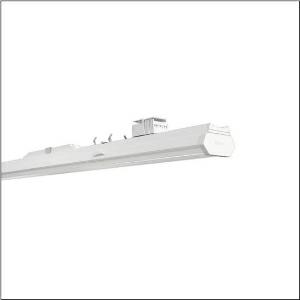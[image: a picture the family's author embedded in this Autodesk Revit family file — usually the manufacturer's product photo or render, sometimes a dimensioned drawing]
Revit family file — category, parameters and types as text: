
# Revit family: licross_21_protected_mo_52tp12mn4a5g
name_source: partatom
category: Lighting Fixtures
units: mm (PartAtom-declared; Revit-internal decimal feet)

## family parameters
Cut with Voids When Loaded = No
Host = Face
Light Source = No
Part Type = Normal
Room Calculation Point = No
Round Connector Dimension = Use Diameter
Shared = No

## types (1)
- --- (1 x LED, 10750 lm, 60.5 W, 4000K)
    Apparent Load = 61 VA
    CIE Flux Codes = 73 92 98 99 100
    Color Rendering = 80
    Color Temperature = 4000K
    Default Elevation = 1800 mm
    Description = Licross 21 Protected MO, luminaire insert, of sheet steel, galvanised, coil coated, white, length: 1.500mm, width: 90mm, height: 101mm, LED rated luminous flux: 10.750lm, light colour: 840, SDCM (Standard Deviation of Colour Matching)MacAdam ≤ 3 SDCM (initial), control gear: ON/OFF Multilumen, with plug, 3-pole, with phase selection, mains connection: 220..240V, AC, 50/60Hz, rated input power: 61W, internal wiring halogen-free, primary light control with lens, of plastic, primary optical cover: cover, of PMMA, light emission: direct distribution, primary light characteristic: symmetric, protection rating (complete): IP64, insulation class (complete): insulation class I (protective earthing), certification: CE, ENEC, VDE, UKCA, protection symbol: D if used in an environment with conductive dust loads with corresponding accessories, impact resistance: IK06, permissible ambient temperature for indoor applications: -35..+45°C, corresponds to IFS (International Featured Standards) requirements for safety and quality in the food industry, reducing of maximum allowable ambient temperature of 5°C with ceiling mounting, LABS conformity tested according to VDMA 24364:2018-05, The light source and the operating device comply with the requirements of the Ecodesign Regulation (EU) 2019/2020 and are replaceable in accordance with this regulation, packaging unit: 1 piece
    Height = 92 mm
    Lamp = 1 x LED
    Lamp Light Flux = 10750 lm
    Lamp Power = 60.5 W
    Lamp count = 1
    Length = 1500 mm
    Luminous efficacy = 178 lm/W
    Manufacturer = Siteco
    ModVariant = No
    Model = 52TP12MN4A5G
    Mounting Place = Ceiling
    Mounting Type = Pendant
    Number of Poles = 1
    OnlyDefault = Yes
    Power Factor = 1
    Product Name = Licross 21 Protected MO
    Product group = luminaire insert | ceiling pendant
    ProductGroupID = 901
    Protection Class = Protection class I
    Protection Degree = IP 64
    RLX_Detail_Level = 1
    RLX_Emergency_Light_Flux = 0 lm
    RLX_Emergency_Type = 0
    RLX_Emergency_Type_DB = No
    RlxData = <blob elided: 22381 chars, md5=a5b52750>
    Socket = socket
    Standby Power = 0 W
    System Light Flux = 10750 lm
    System Power = 61 W
    Type Comments = factory setting: luminous flux: 100 % | (A | C | E) | 140 mA
    Type Image = l_1256148.jpg
    URL = http://relux.com
    VarID = @adj_109071
    Voltage = 0 V
    Weight = 0.00 kg
    Width = 88 mm

## geometry (parser evidence)
native form markers: Blend x4, Sweep x10
no freeform markers — native parametric forms only
